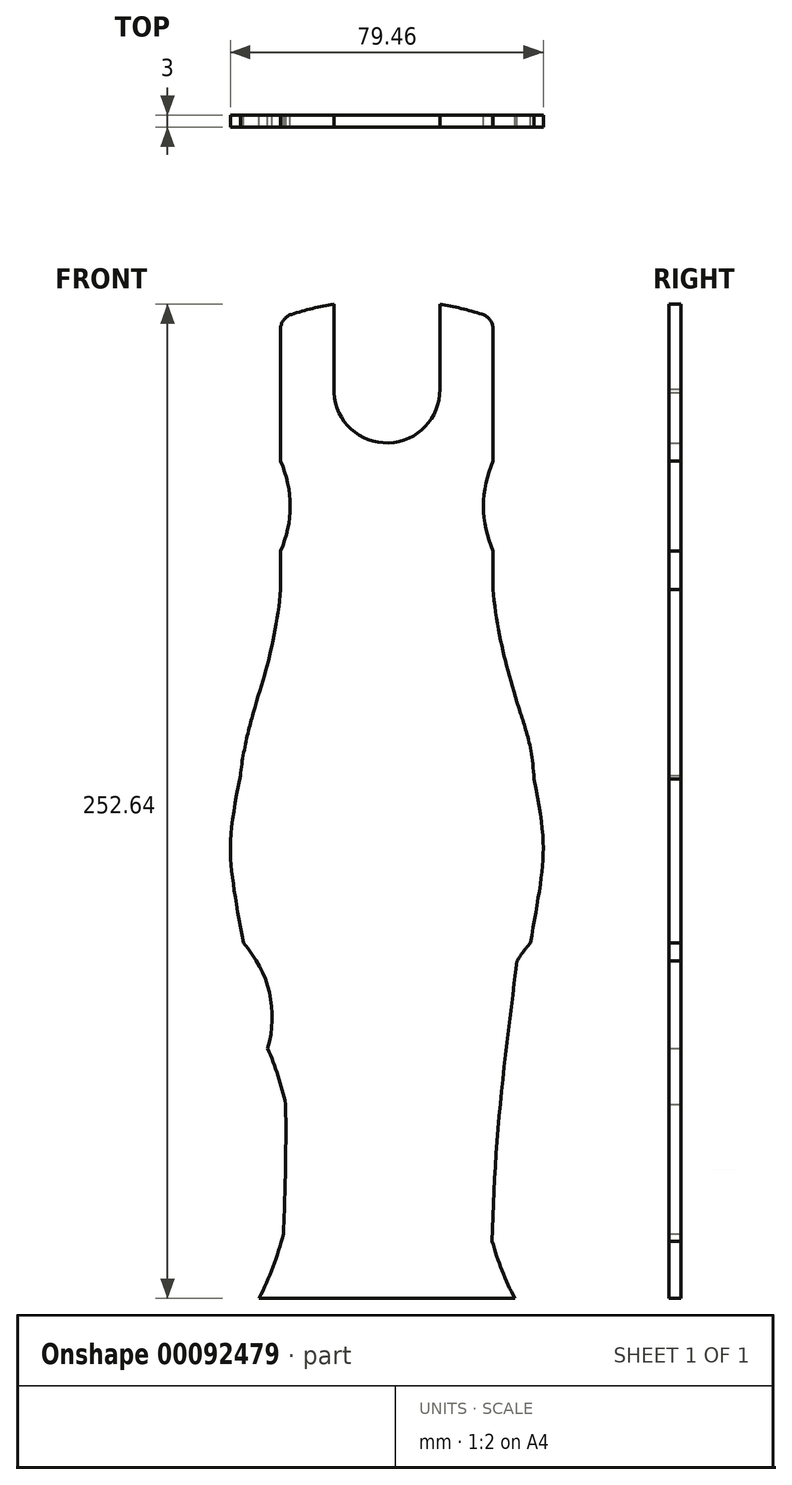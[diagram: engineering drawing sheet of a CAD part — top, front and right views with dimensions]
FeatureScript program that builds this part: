
annotation { "Feature Type Name" : "Feature", "Feature Type Description" : "" }
export const myFeature = defineFeature(function(context is Context, id is Id, definition is map)
    precondition{}
    {
        {
            var Q0;
            Q0=qCreatedBy(makeId("Front.planeOp"),FACE);
            var sketch = newSketch(context, id + "F0", { "sketchPlane" : qUnion([Q0])});
            skLineSegment(sketch, "E0.trimOffspring", {"start": v(-27, 60.5) * mm, "end": v(-27, 70.21) * mm});
            skLineSegment(sketch, "E1.trimOffspring", {"start": v(-27, 67.33) * mm, "end": v(-27, 70.21) * mm});
            skLineSegment(sketch, "E2", {"start": v(-27.02, 97.07) * mm, "end": v(-27.02, 126.57) * mm});
            skFitSpline(sketch, "E3", {"points": [v(-27, 70.21) * mm, v(-27, 60.5) * mm, v(-28.63, 48.92) * mm, v(-30.87, 39.49) * mm, v(-33.96, 28.98) * mm, v(-37.44, 9.05) * mm, v(-35.1, -9.43) * mm, v(-32.97, -21.49) * mm, v(-27, -50.04) * mm, v(-27, -120.02) * mm], "startDerivative": vector(0, -108.37) * mm, "endDerivative": vector(-16.15, -357.79) * mm});
            skArc(sketch, "E4", {"start": v(-13.46, 133) * mm, "mid": v(-18.89, 131.87) * mm, "end": v(-24.23, 130.38) * mm});
            skArc(sketch, "E5.filletArc", {"start": v(-24.23, 130.38) * mm, "mid": v(-26.24, 128.93) * mm, "end": v(-27.02, 126.57) * mm});
            skLineSegment(sketch, "E6", {"start": v(-32.5, -119.64) * mm, "end": v(0, -119.64) * mm});
            skArc(sketch, "E7", {"start": v(-32.5, -119.64) * mm, "mid": v(-24.17, -88.13) * mm, "end": v(-30.27, -56.1) * mm});
            skLineSegment(sketch, "E8.MirrorCS", {"start": v(32.5, -119.64) * mm, "end": v(0, -119.64) * mm});
            skFitSpline(sketch, "E9", {"points": [v(-36.47, -29.38) * mm, v(-39.25, -12.4) * mm, v(-39.43, 0) * mm, v(-33.96, 28.98) * mm], "startDerivative": vector(-10.71, 58.92) * mm, "endDerivative": vector(16.67, 83.84) * mm});
            skLineSegment(sketch, "E10.MirrorCS", {"start": v(-95.06, 60.21) * mm, "end": v(-95.06, 60.21) * mm});
            skPoint(sketch, "E11.visualSharp", {"position": v(-27.02, 93.07) * mm});
            skLineSegment(sketch, "E12.MirrorCS", {"start": v(27.02, 97.07) * mm, "end": v(27.02, 126.57) * mm});
            skArc(sketch, "E13.MirrorCS", {"start": v(24.2, 130.4) * mm, "mid": v(26.24, 128.94) * mm, "end": v(27.02, 126.57) * mm});
            skPoint(sketch, "E14.MirrorP", {"position": v(27.02, 93.07) * mm});
            skLineSegment(sketch, "E15.MirrorCS", {"start": v(95.06, 60.21) * mm, "end": v(95.06, 60.21) * mm});
            skLineSegment(sketch, "E16.MirrorCS", {"start": v(27, 60.5) * mm, "end": v(27, 70.21) * mm});
            skFitSpline(sketch, "E17.MirrorCS", {"points": [v(27, 70.21) * mm, v(27, 60.5) * mm, v(28.63, 48.92) * mm, v(30.87, 39.49) * mm, v(33.96, 28.98) * mm, v(37.44, 9.05) * mm, v(27, -120.02) * mm], "startDerivative": vector(0, -108.37) * mm, "endDerivative": vector(16.15, -357.79) * mm});
            skFitSpline(sketch, "E18.MirrorCS", {"points": [v(36.47, -29.38) * mm, v(39.25, -12.4) * mm, v(39.43, 0) * mm, v(33.96, 28.98) * mm], "startDerivative": vector(10.71, 58.92) * mm, "endDerivative": vector(-16.67, 83.84) * mm});
            skArc(sketch, "E19.MirrorCS", {"start": v(32.5, -119.64) * mm, "mid": v(24.17, -88.13) * mm, "end": v(30.27, -56.1) * mm});
            skPoint(sketch, "E20.end.orphan", {"position": v(0, 134.13) * mm});
            skArc(sketch, "E21.MirrorCS", {"start": v(13.48, 133) * mm, "mid": v(18.88, 131.88) * mm, "end": v(24.2, 130.4) * mm});
            skLineSegment(sketch, "E22", {"start": v(27.02, 97.07) * mm, "end": v(27.01, 93.07) * mm});
            skArc(sketch, "E23", {"start": v(27.02, 93.07) * mm, "mid": v(24.56, 81.65) * mm, "end": v(27, 70.21) * mm});
            skArc(sketch, "E24", {"start": v(36.47, -29.38) * mm, "mid": v(29.86, -41.93) * mm, "end": v(30.27, -56.1) * mm});
            skArc(sketch, "E25.MirrorCS", {"start": v(-27, 93.07) * mm, "mid": v(-24.56, 81.64) * mm, "end": v(-27, 70.21) * mm});
            skArc(sketch, "E26.MirrorCS", {"start": v(-36.47, -29.38) * mm, "mid": v(-29.86, -41.93) * mm, "end": v(-30.27, -56.1) * mm});
            skLineSegment(sketch, "E27", {"start": v(-27, 93.07) * mm, "end": v(-27.02, 97.07) * mm});
            skPoint(sketch, "E28.end.orphan", {"position": v(12.26, 86.01) * mm});
            skArc(sketch, "E29", {"start": v(-13.46, 111.9) * mm, "mid": v(-0.28, 97.7) * mm, "end": v(13.48, 111.33) * mm});
            skLineSegment(sketch, "E30", {"start": v(-13.46, 110.47) * mm, "end": v(-13.46, 133) * mm});
            skLineSegment(sketch, "E31", {"start": v(13.48, 111.33) * mm, "end": v(13.48, 133) * mm});
            skSolve(sketch);
        }
        {
            var Q0;
            Q0 = qSketchRegion(id + "F0", true);
            extrude(context, id + "F1", {"entities" : qUnion([Q0]), "depth" : 3 * mm});
        }
    });
